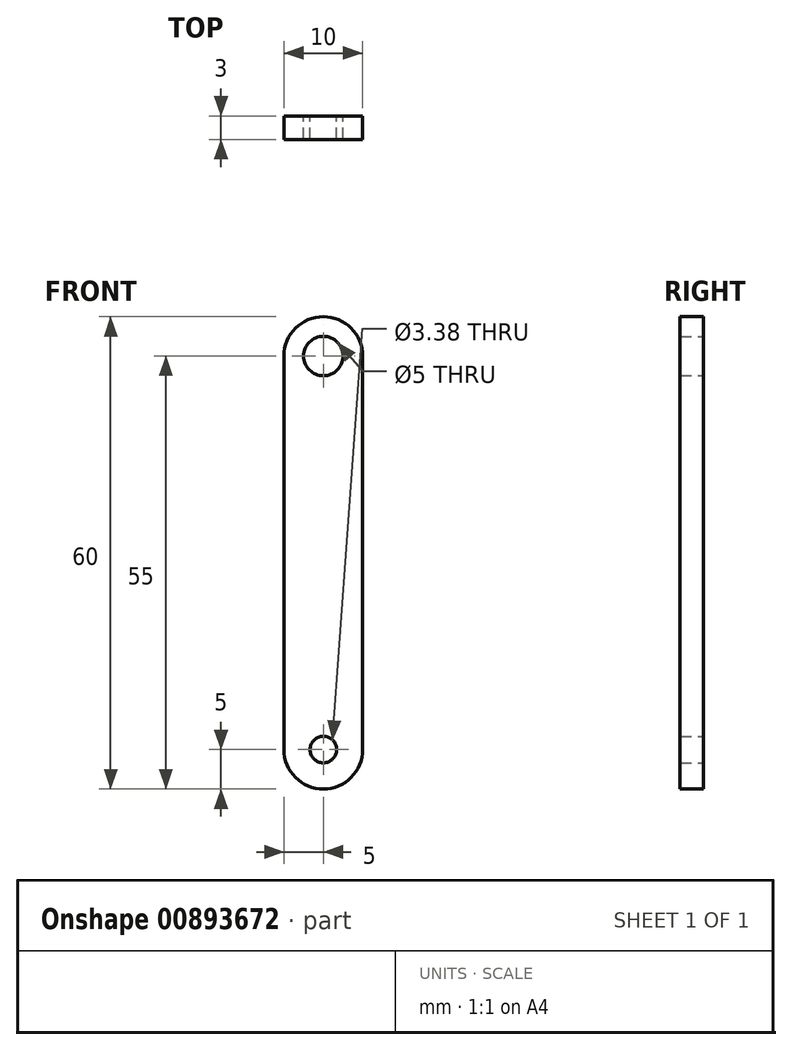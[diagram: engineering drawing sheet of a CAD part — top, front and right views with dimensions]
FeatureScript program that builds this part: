
annotation { "Feature Type Name" : "Feature", "Feature Type Description" : "" }
export const myFeature = defineFeature(function(context is Context, id is Id, definition is map)
    precondition{}
    {
        {
            var Q0;
            Q0=qCreatedBy(makeId("Front.planeOp"),FACE);
            var sketch = newSketch(context, id + "F0", { "sketchPlane" : qUnion([Q0])});
            skLineSegment(sketch, "E0.left", {"start": v(5, -25) * mm, "end": v(5, 25) * mm});
            skLineSegment(sketch, "E0.right", {"start": v(-5, -25) * mm, "end": v(-5, 25) * mm});
            skPoint(sketch, "E0.middle", {"position": v(0, 0) * mm});
            skArc(sketch, "E1", {"start": v(5, 25) * mm, "mid": v(0, 30) * mm, "end": v(-5, 25) * mm});
            skArc(sketch, "E2", {"start": v(-5, -25) * mm, "mid": v(0, -30) * mm, "end": v(5, -25) * mm});
            skCircle(sketch, "E3", {"center": v(0, -25) * mm, "radius": 1.69 * mm});
            skCircle(sketch, "E4", {"center": v(0, 25) * mm, "radius": 2.5 * mm});
            skSolve(sketch);
        }
        {
            var Q0;
            Q0=qSketchRegion(id+"F0",true);
            extrude(context, id + "F1", {"entities" : qUnion([Q0]), "depth" : 3 * mm, "offsetDistance" : 25 * mm});
        }
    });
